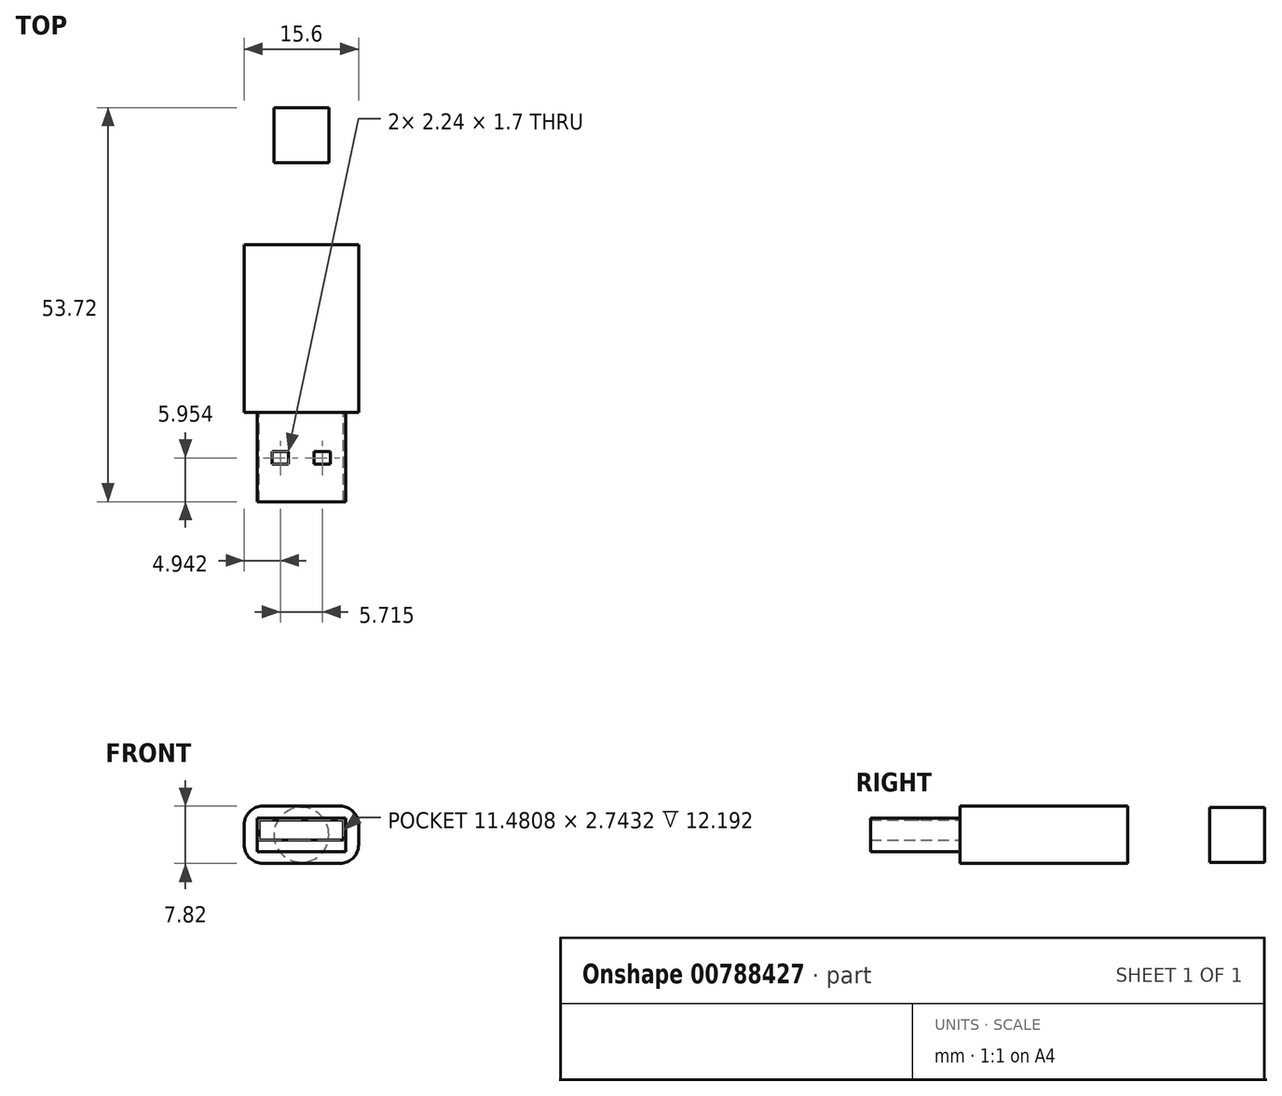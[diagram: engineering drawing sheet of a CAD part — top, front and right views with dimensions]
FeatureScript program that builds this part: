
annotation { "Feature Type Name" : "Feature", "Feature Type Description" : "" }
export const myFeature = defineFeature(function(context is Context, id is Id, definition is map)
    precondition{}
    {
        {
            var Q0;
            Q0=qCreatedBy(makeId("Front.planeOp"),FACE);
            var sketch = newSketch(context, id + "F0", { "sketchPlane" : qUnion([Q0])});
            skLineSegment(sketch, "E0.bottom", {"start": v(6.02, -2.29) * mm, "end": v(-6.02, -2.29) * mm});
            skLineSegment(sketch, "E0.top", {"start": v(6.02, 2.29) * mm, "end": v(-6.02, 2.29) * mm});
            skLineSegment(sketch, "E0.left", {"start": v(6.02, -2.29) * mm, "end": v(6.02, 2.29) * mm});
            skLineSegment(sketch, "E0.right", {"start": v(-6.02, -2.29) * mm, "end": v(-6.02, 2.29) * mm});
            skPoint(sketch, "E0.middle", {"position": v(0, 0) * mm});
            skSolve(sketch);
        }
        {
            var Q0;
            Q0 = qSketchRegion(id + "F0", true);
            extrude(context, id + "F1", {"entities" : qUnion([Q0]), "depth" : 12.2 * mm, "offsetDistance" : 25.4 * mm});
        }
        {
            var Q0;
            Q0=makeQuery(id+"F1.opExtrude","CAP_FACE",FACE,{"disambiguationData":[OSD([sQuery(id+"F0.wireOp",EDGE,"E0.bottom"),sQuery(id+"F0.wireOp",EDGE,"E0.top"),sQuery(id+"F0.wireOp",EDGE,"E0.left"),sQuery(id+"F0.wireOp",EDGE,"E0.right")])],"isStart":false});
            var Q1;
            Q1=makeQuery(id+"F1.opExtrude","CAP_FACE",FACE,{"disambiguationData":[OSD([sQuery(id+"F0.wireOp",EDGE,"E0.bottom"),sQuery(id+"F0.wireOp",EDGE,"E0.top"),sQuery(id+"F0.wireOp",EDGE,"E0.left"),sQuery(id+"F0.wireOp",EDGE,"E0.right")])],"isStart":true});
            shell(context, id + "F2", {"entities" : qUnion([Q0, Q1]), "thickness" : 0.28 * mm});
        }
        {
            var Q0;
            Q0=qCreatedBy(makeId("Front.planeOp"),FACE);
            var sketch = newSketch(context, id + "F3", { "sketchPlane" : qUnion([Q0])});
            skLineSegment(sketch, "E1.bottom", {"start": v(5.26, 3.91) * mm, "end": v(-5.26, 3.91) * mm});
            skLineSegment(sketch, "E1.top", {"start": v(5.26, -3.91) * mm, "end": v(-5.26, -3.91) * mm});
            skLineSegment(sketch, "E1.left", {"start": v(7.8, 1.37) * mm, "end": v(7.8, -1.37) * mm});
            skLineSegment(sketch, "E1.right", {"start": v(-7.8, 1.37) * mm, "end": v(-7.8, -1.37) * mm});
            skPoint(sketch, "E1.middle", {"position": v(0, 0) * mm});
            skPoint(sketch, "E2.visualSharp", {"position": v(-7.8, 3.91) * mm});
            skArc(sketch, "E2.filletArc", {"start": v(-5.26, 3.91) * mm, "mid": v(-7.05, 3.17) * mm, "end": v(-7.8, 1.37) * mm});
            skPoint(sketch, "E3.visualSharp", {"position": v(7.8, 3.91) * mm});
            skArc(sketch, "E3.filletArc", {"start": v(7.8, 1.37) * mm, "mid": v(7.05, 3.17) * mm, "end": v(5.26, 3.91) * mm});
            skPoint(sketch, "E4.visualSharp", {"position": v(7.8, -3.91) * mm});
            skArc(sketch, "E4.filletArc", {"start": v(5.26, -3.91) * mm, "mid": v(7.05, -3.17) * mm, "end": v(7.8, -1.37) * mm});
            skPoint(sketch, "E5.visualSharp", {"position": v(-7.8, -3.91) * mm});
            skArc(sketch, "E5.filletArc", {"start": v(-7.8, -1.37) * mm, "mid": v(-7.05, -3.17) * mm, "end": v(-5.26, -3.91) * mm});
            skSolve(sketch);
        }
        {
            var Q0;
            Q0 = qSketchRegion(id + "F3", true);
            extrude(context, id + "F4", {"entities" : qUnion([Q0]), "operationType" : NewBodyOperationType.ADD, "oppositeDirection" : true, "depth" : 22.86 * mm, "offsetDistance" : 25.4 * mm});
        }
        {
            var Q0;
            Q0=makeQuery(id+"F2.opShell","OFFSET_FACE",FACE,{"disambiguationData":[OSD([sQuery(id+"F0.wireOp",EDGE,"E0.bottom")])]});
            var sketch = newSketch(context, id + "F5", { "sketchPlane" : qUnion([Q0])});
            skLineSegment(sketch, "E6.0", {"start": v(-5.74, -12.2) * mm, "end": v(-5.74, 0) * mm});
            skLineSegment(sketch, "E6.1", {"start": v(5.74, 0) * mm, "end": v(-5.74, 0) * mm});
            skLineSegment(sketch, "E6.2", {"start": v(5.74, -12.2) * mm, "end": v(5.74, 0) * mm});
            skLineSegment(sketch, "E6.3", {"start": v(5.74, -12.2) * mm, "end": v(-5.74, -12.2) * mm});
            skSolve(sketch);
        }
        {
            var Q0;
            Q0=makeQuery(id+"F5.imprint","IMPRINT",FACE,{"disambiguationData":[TD([[makeQuery(id+"F5.imprint","IMPRINT",EDGE,{"derivedFrom":sQuery(id+"F5.wireOp",EDGE,"E6.0")}),-1.0]])]});
            extrude(context, id + "F6", {"entities" : qUnion([Q0]), "operationType" : NewBodyOperationType.ADD, "depth" : 1.27 * mm, "offsetDistance" : 25.4 * mm});
        }
        {
            var Q0;
            Q0=makeQuery(id+"F1.opExtrude","SWEPT_FACE",FACE,{"disambiguationData":[OSD([sQuery(id+"F0.wireOp",EDGE,"E0.top")])]});
            var sketch = newSketch(context, id + "F7", { "sketchPlane" : qUnion([Q0])});
            skLineSegment(sketch, "E7.bottom", {"start": v(-1.74, -7.09) * mm, "end": v(-3.98, -7.09) * mm});
            skLineSegment(sketch, "E7.top", {"start": v(-1.74, -5.38) * mm, "end": v(-3.98, -5.38) * mm});
            skLineSegment(sketch, "E7.left", {"start": v(-1.74, -7.09) * mm, "end": v(-1.74, -5.38) * mm});
            skLineSegment(sketch, "E7.right", {"start": v(-3.98, -7.09) * mm, "end": v(-3.98, -5.38) * mm});
            skPoint(sketch, "E7.middle", {"position": v(-2.86, -6.24) * mm});
            skLineSegment(sketch, "E8.bottom", {"start": v(3.98, -7.09) * mm, "end": v(1.74, -7.09) * mm});
            skLineSegment(sketch, "E8.top", {"start": v(3.98, -5.38) * mm, "end": v(1.74, -5.38) * mm});
            skLineSegment(sketch, "E8.left", {"start": v(3.98, -7.09) * mm, "end": v(3.98, -5.38) * mm});
            skLineSegment(sketch, "E8.right", {"start": v(1.74, -7.09) * mm, "end": v(1.74, -5.38) * mm});
            skPoint(sketch, "E8.middle", {"position": v(2.86, -6.24) * mm});
            skLineSegment(sketch, "E9", {"start": v(0, 0) * mm, "end": v(0, -12.2) * mm, "construction": true});
            skSolve(sketch);
        }
        {
            var Q0;
            Q0 = qSketchRegion(id + "F7", true);
            extrude(context, id + "F8", {"entities" : qUnion([Q0]), "operationType" : NewBodyOperationType.REMOVE, "endBound" : BoundingType.UP_TO_NEXT, "oppositeDirection" : true, "depth" : 25.4 * mm, "offsetDistance" : 25.4 * mm});
        }
        {
            var Q0;
            {var subQ0=sQuery(id+"F3.wireOp",EDGE,"E3.filletArc");var subQ1=sQuery(id+"F3.wireOp",EDGE,"E1.right");var subQ2=sQuery(id+"F3.wireOp",EDGE,"E1.left");var subQ3=sQuery(id+"F3.wireOp",EDGE,"E1.top");var subQ4=sQuery(id+"F3.wireOp",EDGE,"E2.filletArc");var subQ5=sQuery(id+"F3.wireOp",EDGE,"E1.bottom");var subQ6=sQuery(id+"F3.wireOp",EDGE,"E4.filletArc");var subQ7=sQuery(id+"F3.wireOp",EDGE,"E5.filletArc");Q0=makeQuery(id+"F4.boolean.opBoolean","SPLIT",FACE,{"disambiguationData":[TD([makeQuery(id+"F1.opExtrude","SWEPT_FACE",FACE,{"disambiguationData":[OSD([sQuery(id+"F0.wireOp",EDGE,"E0.bottom")])]})])],"derivedFrom":makeQuery(id+"F4.opExtrude","CAP_FACE",FACE,{"disambiguationData":[OSD([subQ5,subQ3,subQ2,subQ1,subQ4,subQ0,subQ6,subQ7])],"isStart":true})});}
            cPlane(context, id + "F9", {"entities" : qUnion([Q0]), "cplaneType" : CPlaneType.OFFSET, "offset" : 41.53 * mm, "oppositeDirection" : true, "width" : 152.4 * mm, "height" : 152.4 * mm});
        }
        {
            var Q0;
            Q0=qCreatedBy(id+"F9.planeOp",FACE);
            var sketch = newSketch(context, id + "F10", { "sketchPlane" : qUnion([Q0])});
            skCircle(sketch, "E10", {"center": v(0, 0) * mm, "radius": 3.75 * mm});
            skSolve(sketch);
        }
        {
            var Q0;
            Q0=makeQuery(id+"F10.imprint","IMPRINT",FACE,{"disambiguationData":[TD([[makeQuery(id+"F10.imprint","IMPRINT",EDGE,{"derivedFrom":sQuery(id+"F10.wireOp",EDGE,"E10")}),1.0]])]});
            extrude(context, id + "F11", {"entities" : qUnion([Q0]), "depth" : 7.5 * mm, "offsetDistance" : 25.4 * mm});
        }
    });
